# Revit family: Gira_003302
name_source: partatom
category: Electrical Fixtures
revit_build: Autodesk Revit 2017 (Build: 20160225_1515(x64)
units: mm (PartAtom-declared; Revit-internal decimal feet)

## family parameters
Cut with Voids When Loaded = No
Host = Face
Maintain Annotation Orientation = Yes
Part Type = Normal
Room Calculation Point = No
Round Connector Dimension = Use Diameter
Shared = No

## types (1)
- TAE-Anschlussdose TAE 3 x 6 NFN Einsatz Weiß
    Abschlusswiderstand = No
    Anschlussart = Schraube
    Aufputz = No
    Auslassrichtung = unten
    Available = Yes
    Befestigungsart = schrauben
    Bodentank/Unterflurmontage = No
    Buchsen geschirmt = Yes
    Category = Kommunikationsanschlussdose Kupfer
    Data sheet (1) = https://katalog.gira.de
    Default Elevation = 1219 mm
    Designfähig = No
    Farbe = sonstige
    GTIN = 4010337034605
    Gehäuse geschirmt = No
    HAN = 003302
    HeinzeBIM = https://bimportal.heinze.de
    Kanaleinbau = No
    Kategorie = sonstige
    Keynote = Einsatz_1fach
    Manufacturer URL = https://www.gira.de
    Mechanische Kodierung = No
    Mit Textfeld = No
    Montageart Schirmanschluss = Schraube
    Name = TAE-Anschlussdose TAE 3 x 6 NFN Einsatz Weiß
    Region = DE
    Schutzart (IP) = IP20
    Separate Kabelzugentlastung = Yes
    Separater Erdungsanschluss = No
    Steckverbindertyp = sonstige
    URL = http://katalog.gira.de
    Unterputz = Yes

## geometry (parser evidence)
native form markers: Blend x2, Sweep x3
no freeform markers — native parametric forms only
